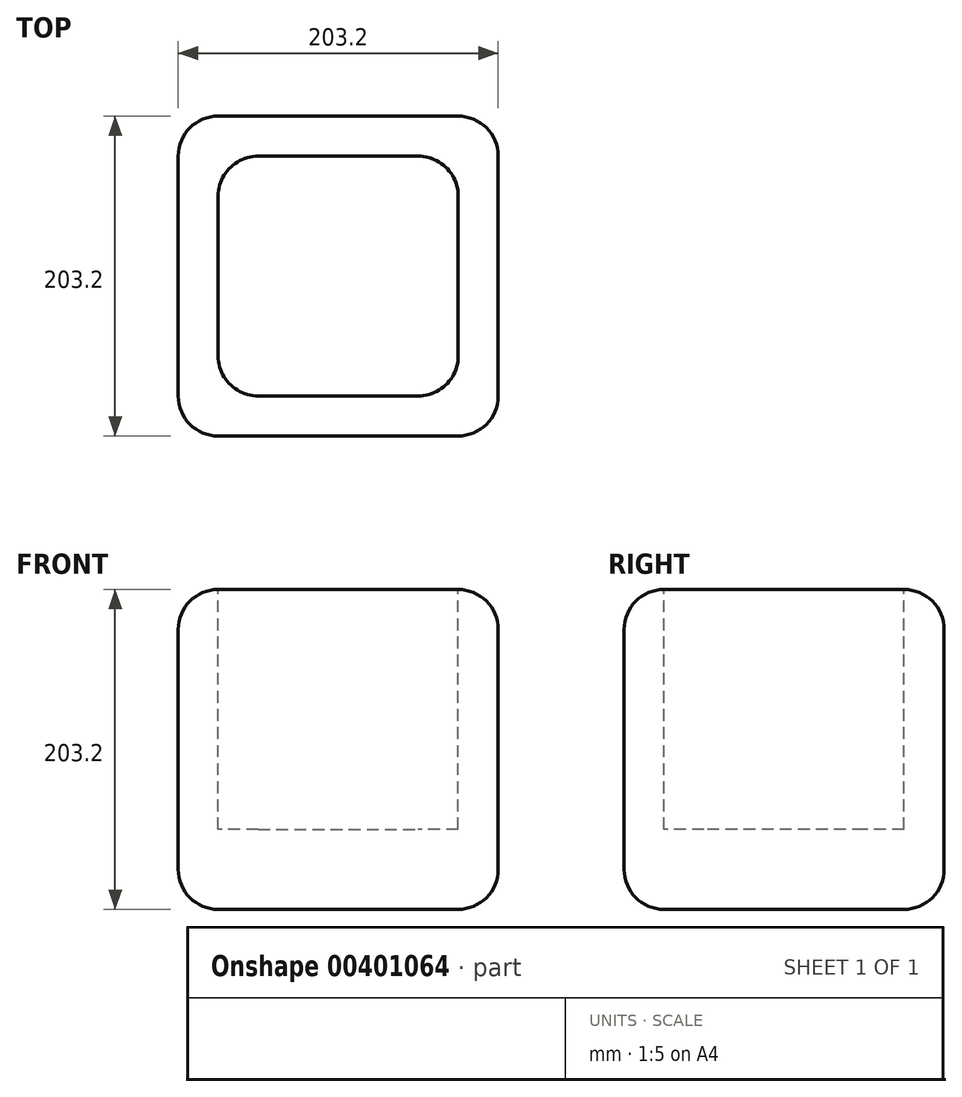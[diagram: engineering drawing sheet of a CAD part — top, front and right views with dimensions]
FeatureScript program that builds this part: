
annotation { "Feature Type Name" : "Feature", "Feature Type Description" : "" }
export const myFeature = defineFeature(function(context is Context, id is Id, definition is map)
    precondition{}
    {
        {
            var Q0;
            Q0=qCreatedBy(makeId("Top.planeOp"),FACE);
            var sketch = newSketch(context, id + "F0", { "sketchPlane" : qUnion([Q0])});
            skLineSegment(sketch, "E0.bottom", {"start": v(-101.6, 101.6) * mm, "end": v(101.6, 101.6) * mm});
            skLineSegment(sketch, "E0.top", {"start": v(-101.6, -101.6) * mm, "end": v(101.6, -101.6) * mm});
            skLineSegment(sketch, "E0.left", {"start": v(-101.6, 101.6) * mm, "end": v(-101.6, -101.6) * mm});
            skLineSegment(sketch, "E0.right", {"start": v(101.6, 101.6) * mm, "end": v(101.6, -101.6) * mm});
            skSolve(sketch);
        }
        {
            var Q0;
            Q0=makeQuery(id+"F0.imprint","IMPRINT",FACE,{"disambiguationData":[TD([[makeQuery(id+"F0.imprint","IMPRINT",EDGE,{"derivedFrom":sQuery(id+"F0.wireOp",EDGE,"E0.bottom")}),-1.0]])]});
            extrude(context, id + "F1", {"entities" : qUnion([Q0]), "depth" : 203.2 * mm});
        }
        {
            var Q0;
            Q0=makeQuery(id+"F1.opExtrude","CAP_FACE",FACE,{"disambiguationData":[OSD([sQuery(id+"F0.wireOp",EDGE,"E0.bottom"),sQuery(id+"F0.wireOp",EDGE,"E0.top"),sQuery(id+"F0.wireOp",EDGE,"E0.left"),sQuery(id+"F0.wireOp",EDGE,"E0.right")])],"isStart":false});
            var Q1;
            Q1=makeQuery(id+"F1.opExtrude","SWEPT_FACE",FACE,{"disambiguationData":[OSD([sQuery(id+"F0.wireOp",EDGE,"E0.top")])]});
            var Q2;
            Q2=makeQuery(id+"F1.opExtrude","SWEPT_FACE",FACE,{"disambiguationData":[OSD([sQuery(id+"F0.wireOp",EDGE,"E0.left")])]});
            var Q3;
            Q3=makeQuery(id+"F1.opExtrude","SWEPT_FACE",FACE,{"disambiguationData":[OSD([sQuery(id+"F0.wireOp",EDGE,"E0.bottom")])]});
            var Q4;
            Q4=makeQuery(id+"F1.opExtrude","SWEPT_FACE",FACE,{"disambiguationData":[OSD([sQuery(id+"F0.wireOp",EDGE,"E0.right")])]});
            var Q5;
            Q5=makeQuery(id+"F1.opExtrude","CAP_FACE",FACE,{"disambiguationData":[OSD([sQuery(id+"F0.wireOp",EDGE,"E0.bottom"),sQuery(id+"F0.wireOp",EDGE,"E0.top"),sQuery(id+"F0.wireOp",EDGE,"E0.left"),sQuery(id+"F0.wireOp",EDGE,"E0.right")])],"isStart":true});
            fillet(context, id + "F2", {"entities" : qUnion([Q0, Q1, Q2, Q3, Q4, Q5]), "radius" : 25.4 * mm, "tangentPropagation" : true, "allowEdgeOverflow" : false});
        }
        {
            var Q0;
            Q0=makeQuery(id+"F1.opExtrude","CAP_FACE",FACE,{"disambiguationData":[OSD([sQuery(id+"F0.wireOp",EDGE,"E0.bottom"),sQuery(id+"F0.wireOp",EDGE,"E0.top"),sQuery(id+"F0.wireOp",EDGE,"E0.left"),sQuery(id+"F0.wireOp",EDGE,"E0.right")])],"isStart":false});
            var sketch = newSketch(context, id + "F3", { "sketchPlane" : qUnion([Q0])});
            skLineSegment(sketch, "E1.0", {"start": v(-25.4, -25.4) * mm, "end": v(25.4, -25.4) * mm});
            skLineSegment(sketch, "E1.1", {"start": v(-25.4, 25.4) * mm, "end": v(-25.4, -25.4) * mm});
            skLineSegment(sketch, "E1.2", {"start": v(25.4, 25.4) * mm, "end": v(-25.4, 25.4) * mm});
            skLineSegment(sketch, "E1.3", {"start": v(25.4, -25.4) * mm, "end": v(25.4, 25.4) * mm});
            skLineSegment(sketch, "E2.bottom", {"start": v(-50.8, 76.2) * mm, "end": v(50.8, 76.2) * mm});
            skLineSegment(sketch, "E2.top", {"start": v(-50.8, -76.2) * mm, "end": v(50.8, -76.2) * mm});
            skLineSegment(sketch, "E2.left", {"start": v(-76.2, 50.8) * mm, "end": v(-76.2, -50.8) * mm});
            skLineSegment(sketch, "E2.right", {"start": v(76.2, 50.8) * mm, "end": v(76.2, -50.8) * mm});
            skPoint(sketch, "E3.visualSharp", {"position": v(-76.2, 76.2) * mm});
            skArc(sketch, "E3.filletArc", {"start": v(-50.8, 76.2) * mm, "mid": v(-68.76, 68.76) * mm, "end": v(-76.2, 50.8) * mm});
            skPoint(sketch, "E4.visualSharp", {"position": v(-76.2, -76.2) * mm});
            skArc(sketch, "E4.filletArc", {"start": v(-76.2, -50.8) * mm, "mid": v(-68.76, -68.76) * mm, "end": v(-50.8, -76.2) * mm});
            skPoint(sketch, "E5.visualSharp", {"position": v(76.2, -76.2) * mm});
            skArc(sketch, "E5.filletArc", {"start": v(50.8, -76.2) * mm, "mid": v(68.76, -68.76) * mm, "end": v(76.2, -50.8) * mm});
            skPoint(sketch, "E6.visualSharp", {"position": v(76.2, 76.2) * mm});
            skArc(sketch, "E6.filletArc", {"start": v(76.2, 50.8) * mm, "mid": v(68.76, 68.76) * mm, "end": v(50.8, 76.2) * mm});
            skSolve(sketch);
        }
        {
            var Q0;
            Q0=makeQuery(id+"F3.imprint","IMPRINT",FACE,{"disambiguationData":[TD([[makeQuery(id+"F3.imprint","IMPRINT",EDGE,{"derivedFrom":sQuery(id+"F3.wireOp",EDGE,"E1.0")}),-1.0]])]});
            extrude(context, id + "F4", {"entities" : qUnion([Q0]), "operationType" : NewBodyOperationType.REMOVE, "oppositeDirection" : true, "depth" : 12.7 * mm});
        }
        {
            var Q0;
            Q0=makeQuery(id+"F1.opExtrude","CAP_FACE",FACE,{"disambiguationData":[OSD([sQuery(id+"F0.wireOp",EDGE,"E0.bottom"),sQuery(id+"F0.wireOp",EDGE,"E0.top"),sQuery(id+"F0.wireOp",EDGE,"E0.left"),sQuery(id+"F0.wireOp",EDGE,"E0.right")])],"isStart":false});
            var sketch = newSketch(context, id + "F5", { "sketchPlane" : qUnion([Q0])});
            skCircle(sketch, "E7", {"center": v(0, 0) * mm, "radius": 35.92 * mm});
            skSolve(sketch);
        }
        {
            var Q0;
            {var subQ1=makeQuery(id+"F4.boolean.opBoolean","COPY",EDGE,{"derivedFrom":makeQuery(id+"F4.opExtrude","CAP_EDGE",EDGE,{"disambiguationData":[OSD([sQuery(id+"F3.wireOp",EDGE,"E1.2")])],"isStart":true})});Q0=makeQuery(id+"F5.imprint","IMPRINT",FACE,{"disambiguationData":[TD([[makeQuery(id+"F5.imprint","IMPRINT",EDGE,{"derivedFrom":subQ1}),-1.0]])]});}
            var Q1;
            {var subQ1=makeQuery(id+"F4.boolean.opBoolean","COPY",EDGE,{"derivedFrom":makeQuery(id+"F4.opExtrude","CAP_EDGE",EDGE,{"disambiguationData":[OSD([sQuery(id+"F3.wireOp",EDGE,"E1.1")])],"isStart":true})});Q1=makeQuery(id+"F5.imprint","IMPRINT",FACE,{"disambiguationData":[TD([[makeQuery(id+"F5.imprint","IMPRINT",EDGE,{"derivedFrom":subQ1}),-1.0]])]});}
            var Q2;
            {var subQ1=makeQuery(id+"F4.boolean.opBoolean","COPY",EDGE,{"derivedFrom":makeQuery(id+"F4.opExtrude","CAP_EDGE",EDGE,{"disambiguationData":[OSD([sQuery(id+"F3.wireOp",EDGE,"E1.0")])],"isStart":true})});Q2=makeQuery(id+"F5.imprint","IMPRINT",FACE,{"disambiguationData":[TD([[makeQuery(id+"F5.imprint","IMPRINT",EDGE,{"derivedFrom":subQ1}),-1.0]])]});}
            var Q3;
            Q3=makeQuery(id+"F5.imprint","IMPRINT",FACE,{"disambiguationData":[TD([[makeQuery(id+"F5.imprint","IMPRINT",EDGE,{"derivedFrom":makeQuery(id+"F4.boolean.opBoolean","COPY",EDGE,{"derivedFrom":makeQuery(id+"F4.opExtrude","CAP_EDGE",EDGE,{"disambiguationData":[OSD([sQuery(id+"F3.wireOp",EDGE,"E1.0")])],"isStart":true})})}),1.0]])]});
            var Q4;
            {var subQ1=makeQuery(id+"F4.boolean.opBoolean","COPY",EDGE,{"derivedFrom":makeQuery(id+"F4.opExtrude","CAP_EDGE",EDGE,{"disambiguationData":[OSD([sQuery(id+"F3.wireOp",EDGE,"E1.3")])],"isStart":true})});Q4=makeQuery(id+"F5.imprint","IMPRINT",FACE,{"disambiguationData":[TD([[makeQuery(id+"F5.imprint","IMPRINT",EDGE,{"derivedFrom":subQ1}),-1.0]])]});}
            extrude(context, id + "F6", {"entities" : qUnion([Q0, Q1, Q2, Q3, Q4]), "operationType" : NewBodyOperationType.REMOVE, "oppositeDirection" : true, "depth" : 12.7 * mm});
        }
        {
            var Q0;
            Q0=makeQuery(id+"F6.boolean.opBoolean","MERGE",FACE,{"derivedFrom":[makeQuery(id+"F4.boolean.opBoolean","COPY",FACE,{"derivedFrom":makeQuery(id+"F4.opExtrude","CAP_FACE",FACE,{"disambiguationData":[OSD([sQuery(id+"F0.wireOp",EDGE,"E0.bottom"),sQuery(id+"F0.wireOp",EDGE,"E0.top"),sQuery(id+"F0.wireOp",EDGE,"E0.left"),sQuery(id+"F0.wireOp",EDGE,"E0.right"),sQuery(id+"F3.wireOp",EDGE,"E1.0"),sQuery(id+"F3.wireOp",EDGE,"E1.1"),sQuery(id+"F3.wireOp",EDGE,"E1.2"),sQuery(id+"F3.wireOp",EDGE,"E1.3")])],"isStart":false})}),makeQuery(id+"F6.opExtrude","CAP_FACE",FACE,{"disambiguationData":[OSD([sQuery(id+"F5.wireOp",EDGE,"E7")])],"isStart":false})]});
            fillet(context, id + "F7", {"entities" : qUnion([Q0]), "radius" : 152.4 * mm, "tangentPropagation" : true, "allowEdgeOverflow" : false});
        }
        {
            var Q0;
            Q0=makeQuery(id+"F6.boolean.opBoolean","MERGE",FACE,{"derivedFrom":[makeQuery(id+"F4.boolean.opBoolean","COPY",FACE,{"derivedFrom":makeQuery(id+"F4.opExtrude","CAP_FACE",FACE,{"disambiguationData":[OSD([sQuery(id+"F3.wireOp",EDGE,"E1.0"),sQuery(id+"F3.wireOp",EDGE,"E1.1"),sQuery(id+"F3.wireOp",EDGE,"E1.2"),sQuery(id+"F3.wireOp",EDGE,"E1.3"),sQuery(id+"F3.wireOp",EDGE,"E2.bottom"),sQuery(id+"F3.wireOp",EDGE,"E2.top"),sQuery(id+"F3.wireOp",EDGE,"E2.left"),sQuery(id+"F3.wireOp",EDGE,"E2.right"),sQuery(id+"F3.wireOp",EDGE,"E3.filletArc"),sQuery(id+"F3.wireOp",EDGE,"E4.filletArc"),sQuery(id+"F3.wireOp",EDGE,"E5.filletArc"),sQuery(id+"F3.wireOp",EDGE,"E6.filletArc")])],"isStart":false})}),makeQuery(id+"F6.opExtrude","CAP_FACE",FACE,{"disambiguationData":[OSD([sQuery(id+"F5.wireOp",EDGE,"E7")])],"isStart":false})]});
            cPlane(context, id + "F8", {"entities" : qUnion([Q0]), "cplaneType" : CPlaneType.OFFSET, "offset" : 25.4 * mm, "oppositeDirection" : true, "width" : 152.4 * mm, "height" : 152.4 * mm});
        }
        {
            var Q0;
            Q0=qCreatedBy(id+"F8.planeOp",FACE);
            var sketch = newSketch(context, id + "F9", { "sketchPlane" : qUnion([Q0])});
            skArc(sketch, "E8", {"start": v(0, 38.1) * mm, "mid": v(-38.1, 0) * mm, "end": v(0, -38.1) * mm});
            skLineSegment(sketch, "E9", {"start": v(0, 38.1) * mm, "end": v(0, -38.1) * mm});
            skSolve(sketch);
        }
        {
            var Q0;
            {var subQ0=sQuery(id+"F0.wireOp",EDGE,"E0.right");var subQ1=sQuery(id+"F0.wireOp",EDGE,"E0.bottom");Q0=makeQuery(id+"F4.boolean.opBoolean","SPLIT",FACE,{"disambiguationData":[TD([makeQuery(id+"F4.opExtrude","SWEPT_FACE",FACE,{"disambiguationData":[OSD([sQuery(id+"F3.wireOp",EDGE,"E6.filletArc")])]})])],"derivedFrom":makeQuery(id+"F1.opExtrude","CAP_FACE",FACE,{"disambiguationData":[OSD([subQ1,sQuery(id+"F0.wireOp",EDGE,"E0.top"),sQuery(id+"F0.wireOp",EDGE,"E0.left"),subQ0])],"isStart":false})});}
            cPlane(context, id + "F10", {"entities" : qUnion([Q0]), "cplaneType" : CPlaneType.OFFSET, "offset" : 25.4 * mm, "width" : 152.4 * mm, "height" : 152.4 * mm});
        }
        {
            var Q0;
            Q0=qCreatedBy(id+"F10.planeOp",FACE);
            var sketch = newSketch(context, id + "F11", { "sketchPlane" : qUnion([Q0])});
            skLineSegment(sketch, "E10.bottom", {"start": v(-50.8, 76.2) * mm, "end": v(50.8, 76.2) * mm});
            skLineSegment(sketch, "E10.top", {"start": v(-50.8, -76.2) * mm, "end": v(50.8, -76.2) * mm});
            skLineSegment(sketch, "E10.left", {"start": v(-76.2, 50.8) * mm, "end": v(-76.2, -50.8) * mm});
            skLineSegment(sketch, "E10.right", {"start": v(76.2, 50.8) * mm, "end": v(76.2, -50.8) * mm});
            skPoint(sketch, "E11.visualSharp", {"position": v(-76.2, 76.2) * mm});
            skArc(sketch, "E11.filletArc", {"start": v(-50.8, 76.2) * mm, "mid": v(-68.76, 68.76) * mm, "end": v(-76.2, 50.8) * mm});
            skPoint(sketch, "E12.visualSharp", {"position": v(-76.2, -76.2) * mm});
            skArc(sketch, "E12.filletArc", {"start": v(-76.2, -50.8) * mm, "mid": v(-68.76, -68.76) * mm, "end": v(-50.8, -76.2) * mm});
            skPoint(sketch, "E13.visualSharp", {"position": v(76.2, -76.2) * mm});
            skArc(sketch, "E13.filletArc", {"start": v(50.8, -76.2) * mm, "mid": v(68.76, -68.76) * mm, "end": v(76.2, -50.8) * mm});
            skPoint(sketch, "E14.visualSharp", {"position": v(76.2, 76.2) * mm});
            skArc(sketch, "E14.filletArc", {"start": v(76.2, 50.8) * mm, "mid": v(68.76, 68.76) * mm, "end": v(50.8, 76.2) * mm});
            skLineSegment(sketch, "E15.0", {"start": v(-50.8, 127) * mm, "end": v(50.8, 127) * mm});
            skArc(sketch, "E15.1", {"start": v(127, 50.8) * mm, "mid": v(104.68, 104.68) * mm, "end": v(50.8, 127) * mm});
            skArc(sketch, "E15.2", {"start": v(-50.8, 127) * mm, "mid": v(-104.68, 104.68) * mm, "end": v(-127, 50.8) * mm});
            skLineSegment(sketch, "E15.3", {"start": v(127, 50.8) * mm, "end": v(127, -50.8) * mm});
            skLineSegment(sketch, "E15.4", {"start": v(-127, 50.8) * mm, "end": v(-127, -50.8) * mm});
            skArc(sketch, "E15.5", {"start": v(-127, -50.8) * mm, "mid": v(-104.68, -104.68) * mm, "end": v(-50.8, -127) * mm});
            skLineSegment(sketch, "E15.6", {"start": v(-50.8, -127) * mm, "end": v(50.8, -127) * mm});
            skArc(sketch, "E15.7", {"start": v(50.8, -127) * mm, "mid": v(104.68, -104.68) * mm, "end": v(127, -50.8) * mm});
            skSolve(sketch);
        }
        {
            var Q0;
            Q0=makeQuery(id+"F11.imprint","IMPRINT",FACE,{"disambiguationData":[TD([[makeQuery(id+"F11.imprint","IMPRINT",EDGE,{"derivedFrom":sQuery(id+"F11.wireOp",EDGE,"E10.bottom")}),-1.0]])]});
            extrude(context, id + "F12", {"entities" : qUnion([Q0]), "operationType" : NewBodyOperationType.REMOVE, "oppositeDirection" : true, "depth" : 177.8 * mm});
        }
    });
